# Revit family: Free_Standing_Tub_Filler-American_Standard-Contemporary_Round-T064951
name_source: partatom
category: Plumbing Fixtures
revit_build: Autodesk Revit 2018 (Build: 20170223_1515(x64)
units: mm (PartAtom-declared; Revit-internal decimal feet)

## family parameters
Always vertical = No
Cut with Voids When Loaded = No
OmniClass Number = 23.45.05.14.21.11
OmniClass Title = Bath/Shower Units
Part Type = Normal
Room Calculation Point = No
Round Connector Dimension = Use Diameter
Shared = Yes
Work Plane-Based = Yes

## types (3) — shared parameters
ADA Compliant = No
Assembly Code = D2020300
CW Connection = Yes
CWFU = 3
Cold Water Connection Diameter = 1/2"
Default Elevation = 0"
Description = T064951 Free Standing Tub Filler Personal Shower. Metal Lever Handle.
Flow Rate = 1.8 gpm (6.8 L/min.)
HW Connection = Yes
HWFU = 3
Height = 47"
Hot Water Connection Diameter = 1"
IAPMO Compliance = ASME A112.18.1, CSA B125.1
Installation Type = Surface Mounted
Length = 11 5/16"
Manufacturer = American Standard
Price = Prices may vary. Please consult Manufacturer Representative for most up-to-date price list.
Product Documentation Link = https://www.americanstandard-us.com
Product Page URL = https://www.americanstandard-us.com
Revised Date = 04/27/2021
Specification = Free standing tub filler shall feature brass construction. Shall also feature 1/4 turn washerless ceramic disc valve cartridge.
Tempered Water Connection Diameter = 1/2"
URL = https://www.americanstandard-us.com
Vent Connection = No
WFU = 4
Warranty Information = Limited Lifetime Warranty
Waste Connection = No
Width = 7"

## per-type parameters (varying)
| type | Finish | Material |
| T064951.002 | Metal-American Standard-002-Polished Chrome | Metal-American Standard-002-Polished Chrome |
| T064951.295 | Metal-American Standard-295-Brushed Nickel | Metal-American Standard-295-Brushed Nickel |
| T064951.243 | Metal-American Standard-243-Matte Black | Metal-American Standard-243-Matte Black |

note: column(s) folded — value = type name in every type: Model

## geometry (parser evidence)
native form markers: Sweep x2
no freeform markers — native parametric forms only
